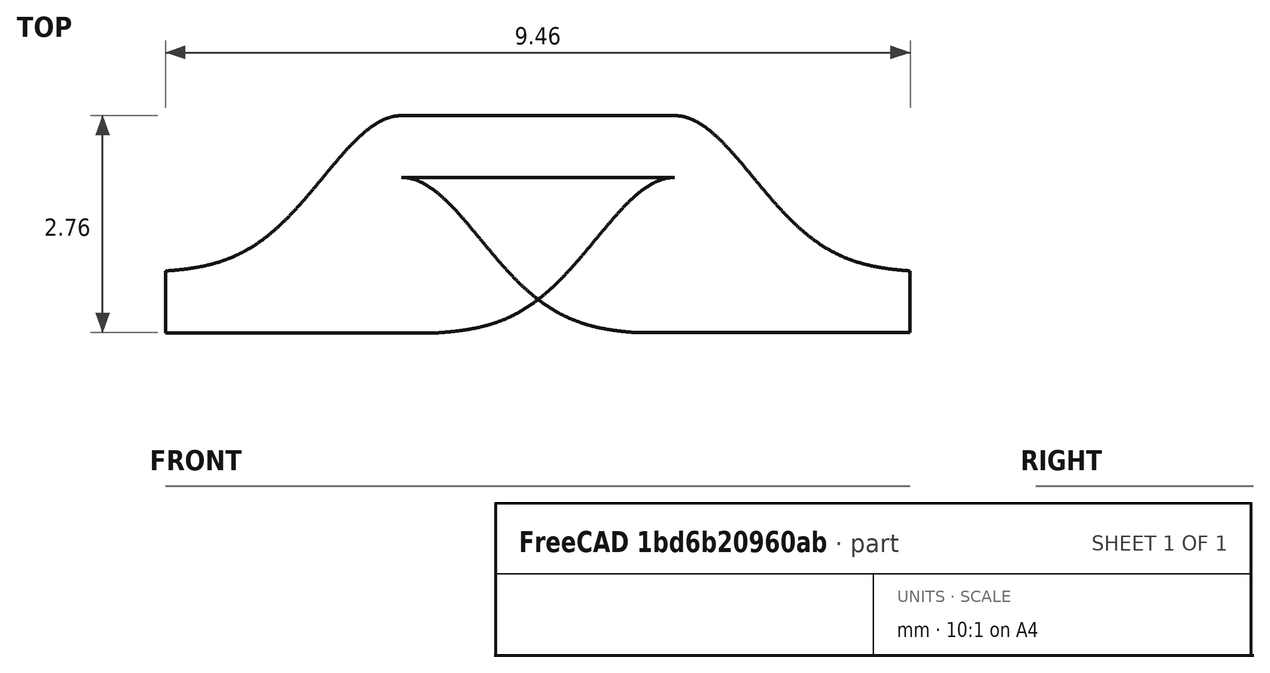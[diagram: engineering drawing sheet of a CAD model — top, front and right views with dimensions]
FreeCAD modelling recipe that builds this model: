
FCSTD DOCUMENT  (FreeCAD 0.20R25352 (Git))
Label: norm-wire
License: All rights reserved
LicenseURL: http://en.wikipedia.org/wiki/All_rights_reserved
objects: PartDesign::AdditivePipe×3, Sketcher::SketchObject×2, Part::Feature×1, PartDesign::Body×1
note: 10 computed .brp shape members not serialized (recipe doc carries the construction recipe); baked Part::Feature solids carry a one-line shape summary decoded from their .brp

FEATURE [Sketcher::SketchObject] Sketch
  FullyConstrained = false
  MapMode = 5
  Placement = pos=(0,0,0) rot=(0.57735,0.57735,0.57735;2.0944rad)
  sketch-geometry (4):
    g0: LineSegment StartX=0 StartY=0 StartZ=0 EndX=1.2656e-11 EndY=0 EndZ=0
    g1: LineSegment StartX=1.2656e-11 StartY=0 StartZ=0 EndX=1.2656e-11 EndY=1.84134 EndZ=0
    g2: LineSegment StartX=1.2656e-11 StartY=1.84134 StartZ=0 EndX=0 EndY=1.84134 EndZ=0
    g3: LineSegment StartX=0 StartY=1.84134 StartZ=0 EndX=0 EndY=0 EndZ=0
  constraints (10):
    c: Coincident(g0,g1)
    c: Coincident(g1,g2)
    c: Coincident(g2,g3)
    c: Coincident(g3,g0)
    c: Horizontal(g0)
    c: Horizontal(g2)
    c: Vertical(g1)
    c: Vertical(g3)
    c: Coincident(g0,g-1)
    c: PointOnObject(g1,g-2)
FEATURE [PartDesign::AdditivePipe] AdditivePipe
  AuxilleryCurvelinear = true
  AuxillerySpineTangent = false
  Binormal = (0,0,0)
  Mode = 0
  Placement = pos=(0,0,0) rot=(0.57735,0.57735,0.57735;2.0944rad)
  Profile = -> Sketch
  Refine = true
  SpineTangent = false
  Transformation = 0
  Transition = 0
FEATURE [PartDesign::AdditivePipe] AdditivePipe001
  AllowMultiFace = false
  AuxilleryCurvelinear = true
  AuxillerySpineTangent = false
  Binormal = (0,0,0)
  Mode = 0
  Refine = true
  SpineTangent = false
  Transformation = 0
  Transition = 0
FEATURE [Sketcher::SketchObject] Sketch001
  FullyConstrained = false
  MapMode = 5
  Support = -> [XY_Plane]
  sketch-geometry (4):
    g0: LineSegment StartX=0 StartY=0 StartZ=0 EndX=3.46601 EndY=0 EndZ=0
    g1: LineSegment StartX=3.46601 StartY=0 StartZ=0 EndX=3.46601 EndY=0.785375 EndZ=0
    g2: LineSegment StartX=3.46601 StartY=0.785375 StartZ=0 EndX=0 EndY=0.785375 EndZ=0
    g3: LineSegment StartX=0 StartY=0.785375 StartZ=0 EndX=0 EndY=0 EndZ=0
  constraints (9):
    c: Coincident(g0,g1)
    c: Coincident(g1,g2)
    c: Coincident(g2,g3)
    c: Coincident(g3,g0)
    c: Horizontal(g0)
    c: Horizontal(g2)
    c: Vertical(g1)
    c: Vertical(g3)
    c: Coincident(g0,g-1)
FEATURE [Part::Feature] Shape
  shape: bbox 5.99 x 1.973 x 2e-07 mm, 0 faces, 0 solids (baked)
FEATURE [PartDesign::AdditivePipe] AdditivePipe002
  AuxilleryCurvelinear = true
  AuxillerySpineTangent = false
  Binormal = (0,0,0)
  Mode = 0
  Profile = -> Sketch001
  Refine = true
  Spine = -> Shape
  SpineTangent = false
  Transformation = 0
  Transition = 0
FEATURE [PartDesign::Body] Body
  Group = -> [Sketch001,AdditivePipe002]
  Origin = -> Origin
  Tip = -> AdditivePipe002
